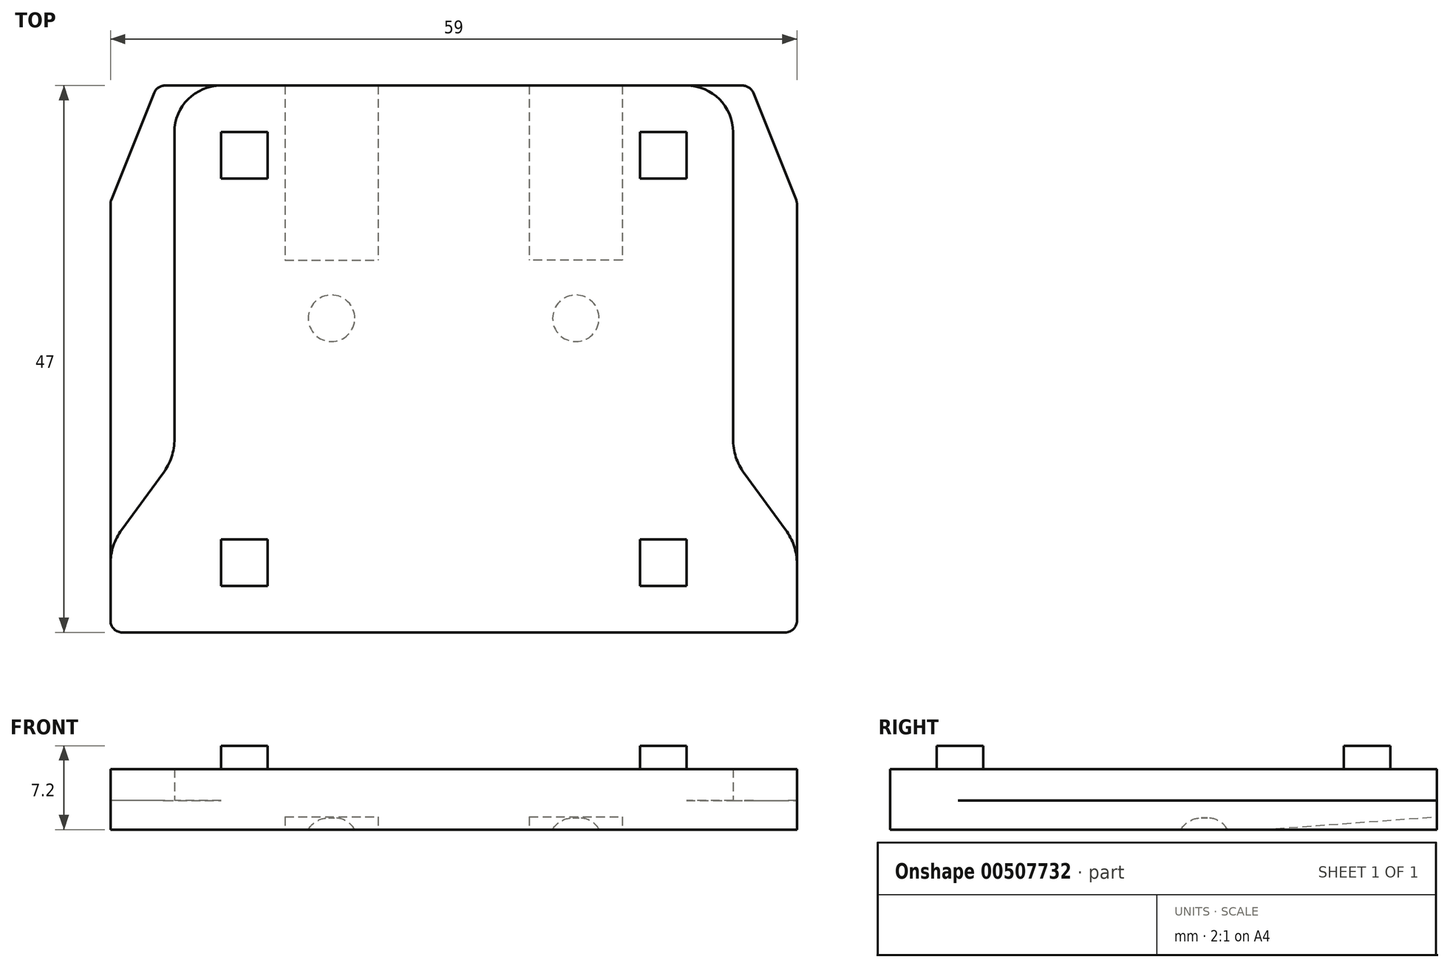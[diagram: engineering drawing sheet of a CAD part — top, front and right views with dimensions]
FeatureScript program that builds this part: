
annotation { "Feature Type Name" : "Feature", "Feature Type Description" : "" }
export const myFeature = defineFeature(function(context is Context, id is Id, definition is map)
    precondition{}
    {
        {
            var Q0;
            Q0=qCreatedBy(makeId("Top.planeOp"),FACE);
            var sketch = newSketch(context, id + "F0", { "sketchPlane" : qUnion([Q0])});
            skLineSegment(sketch, "E0.bottom", {"start": v(4, 0) * mm, "end": v(55, 0) * mm});
            skLineSegment(sketch, "E0.top", {"start": v(0, -47) * mm, "end": v(59, -47) * mm});
            skLineSegment(sketch, "E0.left", {"start": v(0, -10) * mm, "end": v(0, -47) * mm});
            skLineSegment(sketch, "E0.right", {"start": v(59, -10) * mm, "end": v(59, -47) * mm});
            skLineSegment(sketch, "E1", {"start": v(4, 0) * mm, "end": v(0, -10) * mm});
            skPoint(sketch, "E2.orphan", {"position": v(0, 0) * mm});
            skLineSegment(sketch, "E3", {"start": v(55, 0) * mm, "end": v(59, -10) * mm});
            skPoint(sketch, "E4.orphan", {"position": v(59, 0) * mm});
            skSolve(sketch);
        }
        {
            var Q0;
            Q0=makeQuery(id+"F0.imprint","IMPRINT",FACE,{"disambiguationData":[TD([[makeQuery(id+"F0.imprint","IMPRINT",EDGE,{"derivedFrom":sQuery(id+"F0.wireOp",EDGE,"E0.bottom")}),-1.0]])]});
            extrude(context, id + "F1", {"entities" : qUnion([Q0]), "depth" : 2.5 * mm, "offsetDistance" : 25 * mm});
        }
        {
            var Q0;
            Q0=makeQuery(id+"F1.opExtrude","CAP_FACE",FACE,{"disambiguationData":[OSD([sQuery(id+"F0.wireOp",EDGE,"E0.bottom"),sQuery(id+"F0.wireOp",EDGE,"E0.top"),sQuery(id+"F0.wireOp",EDGE,"E0.left"),sQuery(id+"F0.wireOp",EDGE,"E0.right"),sQuery(id+"F0.wireOp",EDGE,"E1"),sQuery(id+"F0.wireOp",EDGE,"E3")])],"isStart":false});
            var sketch = newSketch(context, id + "F2", { "sketchPlane" : qUnion([Q0])});
            skLineSegment(sketch, "E5.bottom", {"start": v(0, -47) * mm, "end": v(59, -47) * mm});
            skLineSegment(sketch, "E5.left", {"start": v(0, -47) * mm, "end": v(0, -39.5) * mm});
            skLineSegment(sketch, "E5.right", {"start": v(59, -47) * mm, "end": v(59, -39.5) * mm});
            skLineSegment(sketch, "E6.top", {"start": v(9.5, 0) * mm, "end": v(49.5, 0) * mm});
            skLineSegment(sketch, "E6.left", {"start": v(5.5, -32) * mm, "end": v(5.5, -4) * mm});
            skLineSegment(sketch, "E6.right", {"start": v(53.5, -32) * mm, "end": v(53.5, -4) * mm});
            skPoint(sketch, "E7.visualSharp", {"position": v(5.5, 0) * mm});
            skArc(sketch, "E7.filletArc", {"start": v(9.5, 0) * mm, "mid": v(6.67, -1.17) * mm, "end": v(5.5, -4) * mm});
            skPoint(sketch, "E8.visualSharp", {"position": v(53.5, 0) * mm});
            skArc(sketch, "E8.filletArc", {"start": v(53.5, -4) * mm, "mid": v(52.33, -1.17) * mm, "end": v(49.5, 0) * mm});
            skLineSegment(sketch, "E9", {"start": v(53.5, -32) * mm, "end": v(59, -39.5) * mm});
            skLineSegment(sketch, "E10", {"start": v(5.5, -32) * mm, "end": v(0, -39.5) * mm});
            skPoint(sketch, "E11.orphan", {"position": v(0, -32) * mm});
            skPoint(sketch, "E12.orphan", {"position": v(59, -32) * mm});
            skSolve(sketch);
        }
        {
            var Q0;
            Q0=makeQuery(id+"F2.imprint","IMPRINT",FACE,{"disambiguationData":[TD([[makeQuery(id+"F2.imprint","IMPRINT",EDGE,{"derivedFrom":sQuery(id+"F2.wireOp",EDGE,"E5.bottom")}),1.0]])]});
            extrude(context, id + "F3", {"entities" : qUnion([Q0]), "operationType" : NewBodyOperationType.ADD, "depth" : 2.7 * mm, "offsetDistance" : 25 * mm});
        }
        {
            var Q0;
            Q0=makeQuery(id+"F3.boolean.opBoolean","MERGE",EDGE,{"derivedFrom":[makeQuery(id+"F1.opExtrude","SWEPT_EDGE",EDGE,{"disambiguationData":[OSD([sQuery(id+"F0.wireOp",EDGE,"E0.top"),sQuery(id+"F0.wireOp",EDGE,"E0.left")])]}),makeQuery(id+"F3.opExtrude","SWEPT_EDGE",EDGE,{"disambiguationData":[OSD([sQuery(id+"F2.wireOp",EDGE,"E5.bottom"),sQuery(id+"F2.wireOp",EDGE,"E5.left")])]})]});
            var Q1;
            Q1=makeQuery(id+"F3.boolean.opBoolean","MERGE",EDGE,{"derivedFrom":[makeQuery(id+"F1.opExtrude","SWEPT_EDGE",EDGE,{"disambiguationData":[OSD([sQuery(id+"F0.wireOp",EDGE,"E0.top"),sQuery(id+"F0.wireOp",EDGE,"E0.right")])]}),makeQuery(id+"F3.opExtrude","SWEPT_EDGE",EDGE,{"disambiguationData":[OSD([sQuery(id+"F2.wireOp",EDGE,"E5.bottom"),sQuery(id+"F2.wireOp",EDGE,"E5.right")])]})]});
            var Q2;
            Q2=makeQuery(id+"F1.opExtrude","SWEPT_EDGE",EDGE,{"disambiguationData":[OSD([sQuery(id+"F0.wireOp",EDGE,"E0.bottom"),sQuery(id+"F0.wireOp",EDGE,"E1")])]});
            var Q3;
            Q3=makeQuery(id+"F1.opExtrude","SWEPT_EDGE",EDGE,{"disambiguationData":[OSD([sQuery(id+"F0.wireOp",EDGE,"E0.bottom"),sQuery(id+"F0.wireOp",EDGE,"E3")])]});
            var Q4;
            Q4=makeQuery(id+"F1.opExtrude","SWEPT_EDGE",EDGE,{"disambiguationData":[OSD([sQuery(id+"F0.wireOp",EDGE,"E0.right"),sQuery(id+"F0.wireOp",EDGE,"E3")])]});
            var Q5;
            Q5=makeQuery(id+"F1.opExtrude","SWEPT_EDGE",EDGE,{"disambiguationData":[OSD([sQuery(id+"F0.wireOp",EDGE,"E0.left"),sQuery(id+"F0.wireOp",EDGE,"E1")])]});
            fillet(context, id + "F4", {"entities" : qUnion([Q0, Q1, Q2, Q3, Q4, Q5]), "radius" : 1 * mm, "tangentPropagation" : true, "allowEdgeOverflow" : false});
        }
        {
            var Q0;
            Q0=makeQuery(id+"F3.opExtrude","SWEPT_EDGE",EDGE,{"disambiguationData":[OSD([sQuery(id+"F0.wireOp",EDGE,"E0.left"),sQuery(id+"F2.wireOp",EDGE,"E5.left"),sQuery(id+"F2.wireOp",EDGE,"E10")])]});
            var Q1;
            Q1=makeQuery(id+"F3.opExtrude","SWEPT_EDGE",EDGE,{"disambiguationData":[OSD([sQuery(id+"F0.wireOp",EDGE,"E0.right"),sQuery(id+"F2.wireOp",EDGE,"E5.right"),sQuery(id+"F2.wireOp",EDGE,"E9")])]});
            var Q2;
            Q2=makeQuery(id+"F3.opExtrude","SWEPT_EDGE",EDGE,{"disambiguationData":[OSD([sQuery(id+"F2.wireOp",EDGE,"E6.right"),sQuery(id+"F2.wireOp",EDGE,"E9")])]});
            var Q3;
            Q3=makeQuery(id+"F3.opExtrude","SWEPT_EDGE",EDGE,{"disambiguationData":[OSD([sQuery(id+"F2.wireOp",EDGE,"E6.left"),sQuery(id+"F2.wireOp",EDGE,"E10")])]});
            fillet(context, id + "F5", {"entities" : qUnion([Q0, Q1, Q2, Q3]), "radius" : 5 * mm, "tangentPropagation" : true, "allowEdgeOverflow" : false});
        }
        {
            var Q0;
            Q0=makeQuery(id+"F1.opExtrude","CAP_FACE",FACE,{"disambiguationData":[OSD([sQuery(id+"F0.wireOp",EDGE,"E0.bottom"),sQuery(id+"F0.wireOp",EDGE,"E0.top"),sQuery(id+"F0.wireOp",EDGE,"E0.left"),sQuery(id+"F0.wireOp",EDGE,"E0.right"),sQuery(id+"F0.wireOp",EDGE,"E1"),sQuery(id+"F0.wireOp",EDGE,"E3")])],"isStart":true});
            var sketch = newSketch(context, id + "F6", { "sketchPlane" : qUnion([Q0])});
            skLineSegment(sketch, "E13.bottom", {"start": v(15, 0) * mm, "end": v(23, 0) * mm});
            skLineSegment(sketch, "E13.top", {"start": v(15, 15) * mm, "end": v(23, 15) * mm});
            skLineSegment(sketch, "E13.left", {"start": v(15, 0) * mm, "end": v(15, 15) * mm});
            skLineSegment(sketch, "E13.right", {"start": v(23, 0) * mm, "end": v(23, 15) * mm});
            skLineSegment(sketch, "E14.bottom", {"start": v(44, 0) * mm, "end": v(36, 0) * mm});
            skLineSegment(sketch, "E14.top", {"start": v(44, 15) * mm, "end": v(36, 15) * mm});
            skLineSegment(sketch, "E14.left", {"start": v(44, 0) * mm, "end": v(44, 15) * mm});
            skLineSegment(sketch, "E14.right", {"start": v(36, 0) * mm, "end": v(36, 15) * mm});
            skSolve(sketch);
        }
        {
            var Q0;
            Q0=makeQuery(id+"F1.opExtrude","CAP_FACE",FACE,{"disambiguationData":[OSD([sQuery(id+"F0.wireOp",EDGE,"E0.bottom"),sQuery(id+"F0.wireOp",EDGE,"E0.top"),sQuery(id+"F0.wireOp",EDGE,"E0.left"),sQuery(id+"F0.wireOp",EDGE,"E0.right"),sQuery(id+"F0.wireOp",EDGE,"E1"),sQuery(id+"F0.wireOp",EDGE,"E3")])],"isStart":true});
            var sketch = newSketch(context, id + "F7", { "sketchPlane" : qUnion([Q0])});
            skCircle(sketch, "E15", {"center": v(19, 20) * mm, "radius": 2 * mm});
            skCircle(sketch, "E16", {"center": v(40, 20) * mm, "radius": 2 * mm});
            skSolve(sketch);
        }
        {
            var Q0;
            Q0=qSketchRegion(id+"F7",true);
            extrude(context, id + "F8", {"entities" : qUnion([Q0]), "operationType" : NewBodyOperationType.REMOVE, "oppositeDirection" : true, "depth" : 1 * mm});
        }
        {
            var Q0;
            Q0=makeQuery(id+"F6.imprint","IMPRINT",FACE,{"disambiguationData":[TD([[makeQuery(id+"F6.imprint","IMPRINT",EDGE,{"derivedFrom":sQuery(id+"F6.wireOp",EDGE,"E14.bottom")}),1.0]])]});
            var Q1;
            Q1=makeQuery(id+"F6.imprint","IMPRINT",FACE,{"disambiguationData":[TD([[makeQuery(id+"F6.imprint","IMPRINT",EDGE,{"derivedFrom":sQuery(id+"F6.wireOp",EDGE,"E13.bottom")}),1.0]])]});
            extrude(context, id + "F9", {"entities" : qUnion([Q0, Q1]), "operationType" : NewBodyOperationType.REMOVE, "oppositeDirection" : true, "depth" : 1.1 * mm});
        }
        {
            var Q0;
            Q0=makeQuery(id+"F9.boolean.opBoolean","COPY",EDGE,{"derivedFrom":makeQuery(id+"F9.opExtrude","CAP_EDGE",EDGE,{"disambiguationData":[OSD([sQuery(id+"F6.wireOp",EDGE,"E13.top")])],"isStart":false})});
            chamfer(context, id + "F10", {"entities" : qUnion([Q0]), "chamferType" : ChamferType.TWO_OFFSETS, "width1" : 1.1 * mm, "oppositeDirection" : false, "width2" : 15 * mm, "tangentPropagation" : true});
        }
        {
            var Q0;
            Q0=makeQuery(id+"F9.boolean.opBoolean","COPY",EDGE,{"derivedFrom":makeQuery(id+"F9.opExtrude","CAP_EDGE",EDGE,{"disambiguationData":[OSD([sQuery(id+"F6.wireOp",EDGE,"E14.top")])],"isStart":false})});
            chamfer(context, id + "F11", {"entities" : qUnion([Q0]), "chamferType" : ChamferType.TWO_OFFSETS, "width1" : 15 * mm, "oppositeDirection" : false, "width2" : 1.1 * mm, "tangentPropagation" : true});
        }
        {
            var Q0;
            Q0=makeQuery(id+"F8.boolean.opBoolean","COPY",EDGE,{"derivedFrom":makeQuery(id+"F8.opExtrude","CAP_EDGE",EDGE,{"disambiguationData":[OSD([sQuery(id+"F7.wireOp",EDGE,"E16")])],"isStart":false})});
            var Q1;
            Q1=makeQuery(id+"F8.boolean.opBoolean","COPY",EDGE,{"derivedFrom":makeQuery(id+"F8.opExtrude","CAP_EDGE",EDGE,{"disambiguationData":[OSD([sQuery(id+"F7.wireOp",EDGE,"E15")])],"isStart":false})});
            fillet(context, id + "F12", {"entities" : qUnion([Q0, Q1]), "radius" : 2 * mm, "tangentPropagation" : true, "allowEdgeOverflow" : false});
        }
        {
            var Q0;
            Q0=makeQuery(id+"F3.opExtrude","CAP_FACE",FACE,{"disambiguationData":[OSD([sQuery(id+"F2.wireOp",EDGE,"E5.bottom"),sQuery(id+"F2.wireOp",EDGE,"E5.left"),sQuery(id+"F2.wireOp",EDGE,"E5.right"),sQuery(id+"F2.wireOp",EDGE,"E6.top"),sQuery(id+"F2.wireOp",EDGE,"E6.left"),sQuery(id+"F2.wireOp",EDGE,"E6.right"),sQuery(id+"F2.wireOp",EDGE,"E7.filletArc"),sQuery(id+"F2.wireOp",EDGE,"E8.filletArc"),sQuery(id+"F2.wireOp",EDGE,"E9"),sQuery(id+"F2.wireOp",EDGE,"E10")])],"isStart":false});
            var sketch = newSketch(context, id + "F13", { "sketchPlane" : qUnion([Q0])});
            skLineSegment(sketch, "E17.bottom", {"start": v(9.5, -4) * mm, "end": v(13.5, -4) * mm});
            skLineSegment(sketch, "E17.top", {"start": v(9.5, -8) * mm, "end": v(13.5, -8) * mm});
            skLineSegment(sketch, "E17.left", {"start": v(9.5, -4) * mm, "end": v(9.5, -8) * mm});
            skLineSegment(sketch, "E17.right", {"start": v(13.5, -4) * mm, "end": v(13.5, -8) * mm});
            skLineSegment(sketch, "E18.bottom", {"start": v(9.5, -39) * mm, "end": v(13.5, -39) * mm});
            skLineSegment(sketch, "E18.top", {"start": v(9.5, -43) * mm, "end": v(13.5, -43) * mm});
            skLineSegment(sketch, "E18.left", {"start": v(9.5, -39) * mm, "end": v(9.5, -43) * mm});
            skLineSegment(sketch, "E18.right", {"start": v(13.5, -39) * mm, "end": v(13.5, -43) * mm});
            skLineSegment(sketch, "E19.bottom", {"start": v(45.5, -4) * mm, "end": v(49.5, -4) * mm});
            skLineSegment(sketch, "E19.top", {"start": v(45.5, -8) * mm, "end": v(49.5, -8) * mm});
            skLineSegment(sketch, "E19.left", {"start": v(45.5, -4) * mm, "end": v(45.5, -8) * mm});
            skLineSegment(sketch, "E19.right", {"start": v(49.5, -4) * mm, "end": v(49.5, -8) * mm});
            skLineSegment(sketch, "E20.bottom", {"start": v(45.5, -39) * mm, "end": v(49.5, -39) * mm});
            skLineSegment(sketch, "E20.top", {"start": v(45.5, -43) * mm, "end": v(49.5, -43) * mm});
            skLineSegment(sketch, "E20.left", {"start": v(45.5, -39) * mm, "end": v(45.5, -43) * mm});
            skLineSegment(sketch, "E20.right", {"start": v(49.5, -39) * mm, "end": v(49.5, -43) * mm});
            skSolve(sketch);
        }
        {
            var Q0;
            Q0=qSketchRegion(id+"F13",true);
            extrude(context, id + "F14", {"entities" : qUnion([Q0]), "operationType" : NewBodyOperationType.ADD, "depth" : 2 * mm, "offsetDistance" : 25 * mm});
        }
    });
